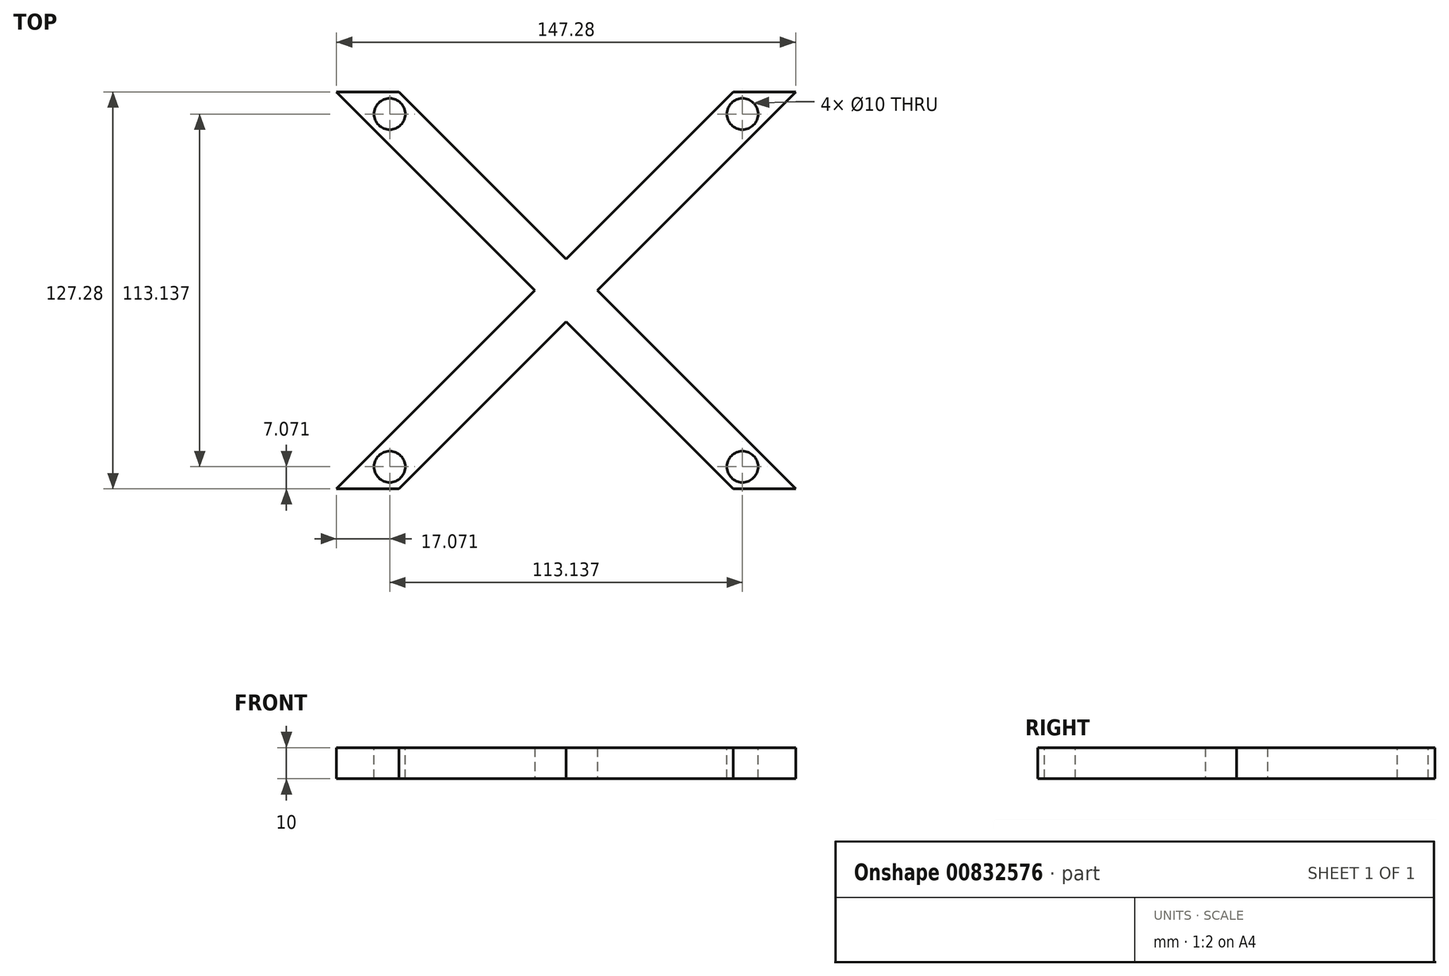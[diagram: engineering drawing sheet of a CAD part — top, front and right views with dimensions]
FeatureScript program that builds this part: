
annotation { "Feature Type Name" : "Feature", "Feature Type Description" : "" }
export const myFeature = defineFeature(function(context is Context, id is Id, definition is map)
    precondition{}
    {
        {
            var Q0;
            Q0=qCreatedBy(makeId("Top.planeOp"),FACE);
            var sketch = newSketch(context, id + "F0", { "sketchPlane" : qUnion([Q0])});
            skLineSegment(sketch, "E0", {"start": v(0, 0) * mm, "end": v(127.28, 127.28) * mm, "construction": true});
            skLineSegment(sketch, "E1", {"start": v(0, 127.28) * mm, "end": v(127.28, 0) * mm, "construction": true});
            skLineSegment(sketch, "E2", {"start": v(-10, 127.28) * mm, "end": v(10, 127.28) * mm});
            skLineSegment(sketch, "E3", {"start": v(117.28, 0) * mm, "end": v(137.28, 0) * mm});
            skLineSegment(sketch, "E4", {"start": v(10, 127.28) * mm, "end": v(137.28, 0) * mm});
            skLineSegment(sketch, "E5", {"start": v(117.28, 0) * mm, "end": v(-10, 127.28) * mm});
            skLineSegment(sketch, "E6", {"start": v(117.28, 127.28) * mm, "end": v(137.28, 127.28) * mm});
            skLineSegment(sketch, "E7", {"start": v(-10, 0) * mm, "end": v(10, 0) * mm});
            skLineSegment(sketch, "E8", {"start": v(-10, 0) * mm, "end": v(117.28, 127.28) * mm});
            skLineSegment(sketch, "E9", {"start": v(137.28, 127.28) * mm, "end": v(10, 0) * mm});
            skSolve(sketch);
        }
        {
            var Q0;
            {var subQ0=sQuery(id+"F0.wireOp",EDGE,"E2");Q0=makeQuery(id+"F0.imprint","IMPRINT",FACE,{"disambiguationData":[TD([[makeQuery(id+"F0.imprint","IMPRINT",EDGE,{"derivedFrom":subQ0}),-1.0]])]});}
            var Q1;
            {var subQ0=sQuery(id+"F0.wireOp",EDGE,"E8");var subQ1=sQuery(id+"F0.wireOp",EDGE,"E4");var subQ2=makeQuery(id+"F0.imprint","INTERSECT",VERTEX,{"derivedFrom":[subQ1,subQ0]});Q1=makeQuery(id+"F0.imprint","IMPRINT",FACE,{"disambiguationData":[TD([[makeQuery(id+"F0.imprint","IMPRINT",EDGE,{"disambiguationData":[TD([[subQ2,-1.0]])],"derivedFrom":subQ1}),-1.0]])]});}
            var Q2;
            {var subQ5=sQuery(id+"F0.wireOp",EDGE,"E6");Q2=makeQuery(id+"F0.imprint","IMPRINT",FACE,{"disambiguationData":[TD([[makeQuery(id+"F0.imprint","IMPRINT",EDGE,{"derivedFrom":subQ5}),-1.0]])]});}
            var Q3;
            {var subQ0=sQuery(id+"F0.wireOp",EDGE,"E3");Q3=makeQuery(id+"F0.imprint","IMPRINT",FACE,{"disambiguationData":[TD([[makeQuery(id+"F0.imprint","IMPRINT",EDGE,{"derivedFrom":subQ0}),1.0]])]});}
            var Q4;
            {var subQ5=sQuery(id+"F0.wireOp",EDGE,"E7");Q4=makeQuery(id+"F0.imprint","IMPRINT",FACE,{"disambiguationData":[TD([[makeQuery(id+"F0.imprint","IMPRINT",EDGE,{"derivedFrom":subQ5}),1.0]])]});}
            extrude(context, id + "F1", {"entities" : qUnion([Q0, Q1, Q2, Q3, Q4]), "depth" : 10 * mm, "offsetDistance" : 25 * mm});
        }
        {
            var Q0;
            Q0=makeQuery(id+"F1.opExtrude","CAP_FACE",FACE,{"disambiguationData":[OSD([sQuery(id+"F0.wireOp",EDGE,"E2"),sQuery(id+"F0.wireOp",EDGE,"E3"),sQuery(id+"F0.wireOp",EDGE,"E4"),sQuery(id+"F0.wireOp",EDGE,"E5"),sQuery(id+"F0.wireOp",EDGE,"E6"),sQuery(id+"F0.wireOp",EDGE,"E7"),sQuery(id+"F0.wireOp",EDGE,"E8"),sQuery(id+"F0.wireOp",EDGE,"E9")])],"isStart":false});
            var sketch = newSketch(context, id + "F2", { "sketchPlane" : qUnion([Q0])});
            skCircle(sketch, "E10", {"center": v(7.07, 7.07) * mm, "radius": 5 * mm});
            skCircle(sketch, "E11", {"center": v(120.2, 7.07) * mm, "radius": 5 * mm});
            skCircle(sketch, "E12", {"center": v(120.2, 120.2) * mm, "radius": 5 * mm});
            skCircle(sketch, "E13", {"center": v(7.07, 120.2) * mm, "radius": 5 * mm});
            skSolve(sketch);
        }
        {
            var Q0;
            Q0=makeQuery(id+"F2.imprint","IMPRINT",FACE,{"disambiguationData":[TD([[makeQuery(id+"F2.imprint","IMPRINT",EDGE,{"derivedFrom":sQuery(id+"F2.wireOp",EDGE,"E13")}),1.0]])]});
            var Q1;
            Q1=makeQuery(id+"F2.imprint","IMPRINT",FACE,{"disambiguationData":[TD([[makeQuery(id+"F2.imprint","IMPRINT",EDGE,{"derivedFrom":sQuery(id+"F2.wireOp",EDGE,"E12")}),1.0]])]});
            var Q2;
            Q2=makeQuery(id+"F2.imprint","IMPRINT",FACE,{"disambiguationData":[TD([[makeQuery(id+"F2.imprint","IMPRINT",EDGE,{"derivedFrom":sQuery(id+"F2.wireOp",EDGE,"E11")}),1.0]])]});
            var Q3;
            Q3=makeQuery(id+"F2.imprint","IMPRINT",FACE,{"disambiguationData":[TD([[makeQuery(id+"F2.imprint","IMPRINT",EDGE,{"derivedFrom":sQuery(id+"F2.wireOp",EDGE,"E10")}),1.0]])]});
            extrude(context, id + "F3", {"entities" : qUnion([Q0, Q1, Q2, Q3]), "operationType" : NewBodyOperationType.REMOVE, "oppositeDirection" : true, "depth" : 25 * mm, "offsetDistance" : 25 * mm});
        }
    });
